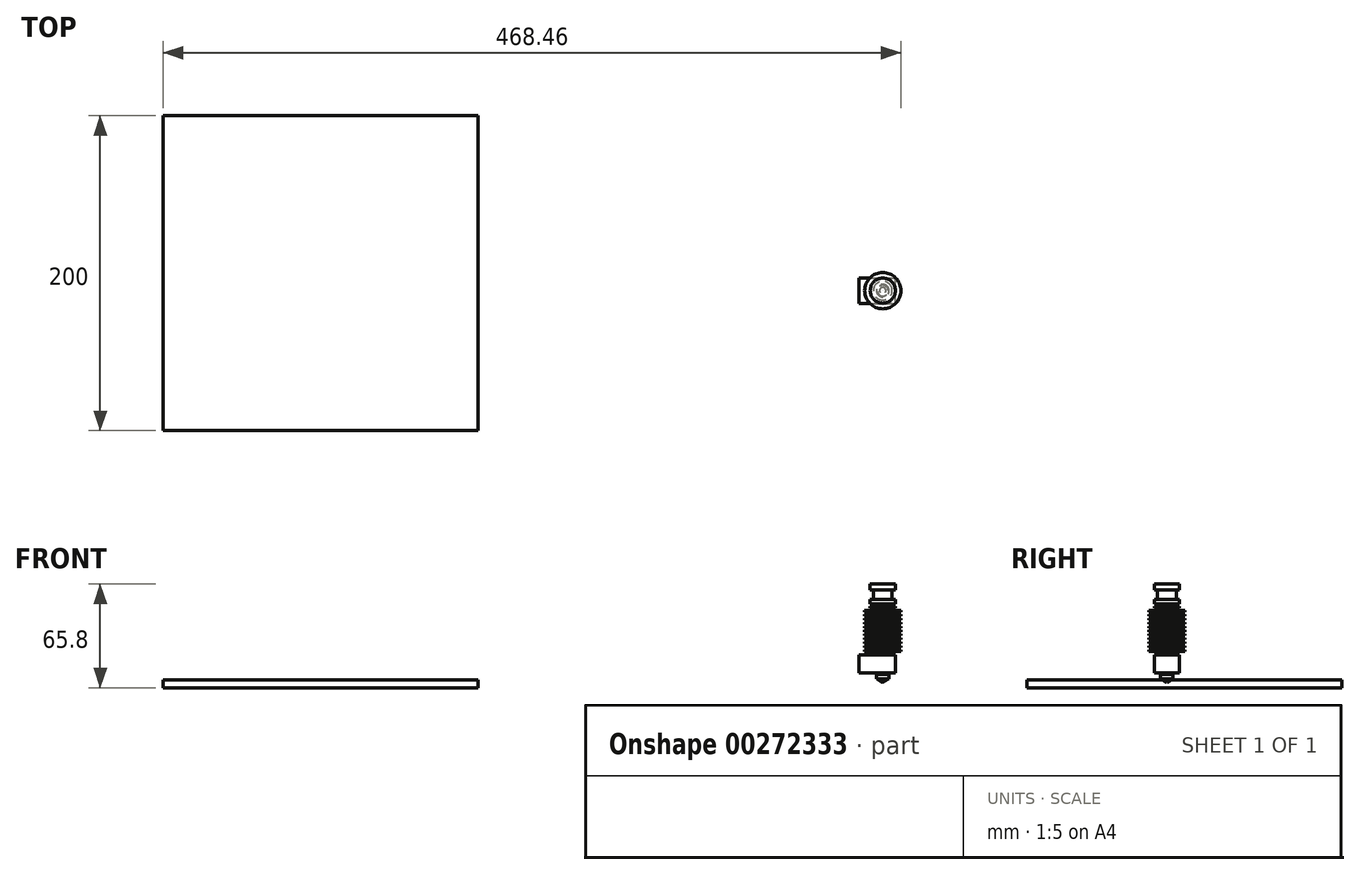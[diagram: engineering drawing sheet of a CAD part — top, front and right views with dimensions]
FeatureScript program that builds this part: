
annotation { "Feature Type Name" : "Feature", "Feature Type Description" : "" }
export const myFeature = defineFeature(function(context is Context, id is Id, definition is map)
    precondition{}
    {
        {
            var Q0;
            Q0=qCreatedBy(makeId("Front.planeOp"),FACE);
            var sketch = newSketch(context, id + "F0", { "sketchPlane" : qUnion([Q0])});
            skLineSegment(sketch, "E0", {"start": v(-127.3, 65.8) * mm, "end": v(-127.3, 23.1) * mm});
            skLineSegment(sketch, "E1", {"start": v(-127.3, 65.8) * mm, "end": v(-119.3, 65.8) * mm});
            skLineSegment(sketch, "E2", {"start": v(-119.3, 65.8) * mm, "end": v(-119.3, 62.1) * mm});
            skLineSegment(sketch, "E3", {"start": v(-119.3, 62.1) * mm, "end": v(-121.3, 62.1) * mm});
            skLineSegment(sketch, "E4", {"start": v(-121.3, 62.1) * mm, "end": v(-121.3, 56.1) * mm});
            skLineSegment(sketch, "E5", {"start": v(-121.3, 56.1) * mm, "end": v(-119.3, 56.1) * mm});
            skLineSegment(sketch, "E6", {"start": v(-119.3, 56.1) * mm, "end": v(-119.3, 53.1) * mm});
            skLineSegment(sketch, "E7", {"start": v(-119.3, 53.1) * mm, "end": v(-121.3, 53.1) * mm});
            skLineSegment(sketch, "E8", {"start": v(-121.3, 53.1) * mm, "end": v(-121.3, 51.6) * mm});
            skLineSegment(sketch, "E9", {"start": v(-121.3, 51.6) * mm, "end": v(-119.3, 51.6) * mm});
            skLineSegment(sketch, "E10", {"start": v(-119.3, 51.6) * mm, "end": v(-119.3, 50.6) * mm});
            skLineSegment(sketch, "E11", {"start": v(-119.3, 50.6) * mm, "end": v(-121.3, 50.6) * mm});
            skLineSegment(sketch, "E12", {"start": v(-121.3, 50.6) * mm, "end": v(-121.3, 49.1) * mm});
            skLineSegment(sketch, "E13", {"start": v(-121.3, 49.1) * mm, "end": v(-115.8, 49.1) * mm});
            skLineSegment(sketch, "E14", {"start": v(-115.8, 49.1) * mm, "end": v(-115.8, 48.1) * mm});
            skLineSegment(sketch, "E15", {"start": v(-115.8, 48.1) * mm, "end": v(-121.3, 48.1) * mm});
            skLineSegment(sketch, "E16.1.0.1", {"start": v(-121.3, 46.6) * mm, "end": v(-115.8, 46.6) * mm});
            skLineSegment(sketch, "E16.1.0.2", {"start": v(-115.8, 46.6) * mm, "end": v(-115.8, 45.6) * mm});
            skLineSegment(sketch, "E16.1.0.3", {"start": v(-115.8, 45.6) * mm, "end": v(-121.3, 45.6) * mm});
            skLineSegment(sketch, "E16.2.0.0", {"start": v(-121.3, 45.6) * mm, "end": v(-121.3, 44.1) * mm});
            skLineSegment(sketch, "E16.2.0.1", {"start": v(-121.3, 44.1) * mm, "end": v(-115.8, 44.1) * mm});
            skLineSegment(sketch, "E16.2.0.2", {"start": v(-115.8, 44.1) * mm, "end": v(-115.8, 43.1) * mm});
            skLineSegment(sketch, "E16.2.0.3", {"start": v(-115.8, 43.1) * mm, "end": v(-121.3, 43.1) * mm});
            skLineSegment(sketch, "E16.direction1", {"start": v(-121.3, 48.1) * mm, "end": v(-121.3, 45.6) * mm, "construction": true});
            skLineSegment(sketch, "E17.0.3.0", {"start": v(-121.3, 43.1) * mm, "end": v(-121.3, 41.6) * mm});
            skLineSegment(sketch, "E17.3.3.0", {"start": v(-121.3, 41.6) * mm, "end": v(-115.8, 41.6) * mm});
            skLineSegment(sketch, "E17.6.3.0", {"start": v(-115.8, 41.6) * mm, "end": v(-115.8, 40.6) * mm});
            skLineSegment(sketch, "E17.9.3.0", {"start": v(-115.8, 40.6) * mm, "end": v(-121.3, 40.6) * mm});
            skLineSegment(sketch, "E17.0.4.0", {"start": v(-121.3, 40.6) * mm, "end": v(-121.3, 39.1) * mm});
            skLineSegment(sketch, "E17.3.4.0", {"start": v(-121.3, 39.1) * mm, "end": v(-115.8, 39.1) * mm});
            skLineSegment(sketch, "E17.6.4.0", {"start": v(-115.8, 39.1) * mm, "end": v(-115.8, 38.1) * mm});
            skLineSegment(sketch, "E17.9.4.0", {"start": v(-115.8, 38.1) * mm, "end": v(-121.3, 38.1) * mm});
            skLineSegment(sketch, "E17.0.5.0", {"start": v(-121.3, 38.1) * mm, "end": v(-121.3, 36.6) * mm});
            skLineSegment(sketch, "E17.3.5.0", {"start": v(-121.3, 36.6) * mm, "end": v(-115.8, 36.6) * mm});
            skLineSegment(sketch, "E17.6.5.0", {"start": v(-115.8, 36.6) * mm, "end": v(-115.8, 35.6) * mm});
            skLineSegment(sketch, "E17.9.5.0", {"start": v(-115.8, 35.6) * mm, "end": v(-121.3, 35.6) * mm});
            skLineSegment(sketch, "E17.0.6.0", {"start": v(-121.3, 35.6) * mm, "end": v(-121.3, 34.1) * mm});
            skLineSegment(sketch, "E17.3.6.0", {"start": v(-121.3, 34.1) * mm, "end": v(-115.8, 34.1) * mm});
            skLineSegment(sketch, "E17.6.6.0", {"start": v(-115.8, 34.1) * mm, "end": v(-115.8, 33.1) * mm});
            skLineSegment(sketch, "E17.9.6.0", {"start": v(-115.8, 33.1) * mm, "end": v(-121.3, 33.1) * mm});
            skLineSegment(sketch, "E17.0.7.0", {"start": v(-121.3, 33.1) * mm, "end": v(-121.3, 31.6) * mm});
            skLineSegment(sketch, "E17.3.7.0", {"start": v(-121.3, 31.6) * mm, "end": v(-115.8, 31.6) * mm});
            skLineSegment(sketch, "E17.6.7.0", {"start": v(-115.8, 31.6) * mm, "end": v(-115.8, 30.6) * mm});
            skLineSegment(sketch, "E17.9.7.0", {"start": v(-115.8, 30.6) * mm, "end": v(-121.3, 30.6) * mm});
            skLineSegment(sketch, "E17.0.8.0", {"start": v(-121.3, 30.6) * mm, "end": v(-121.3, 29.1) * mm});
            skLineSegment(sketch, "E17.3.8.0", {"start": v(-121.3, 29.1) * mm, "end": v(-115.8, 29.1) * mm});
            skLineSegment(sketch, "E17.6.8.0", {"start": v(-115.8, 29.1) * mm, "end": v(-115.8, 28.1) * mm});
            skLineSegment(sketch, "E17.9.8.0", {"start": v(-115.8, 28.1) * mm, "end": v(-121.3, 28.1) * mm});
            skLineSegment(sketch, "E17.0.9.0", {"start": v(-121.3, 28.1) * mm, "end": v(-121.3, 26.6) * mm});
            skLineSegment(sketch, "E17.3.9.0", {"start": v(-121.3, 26.6) * mm, "end": v(-115.8, 26.6) * mm});
            skLineSegment(sketch, "E17.6.9.0", {"start": v(-115.8, 26.6) * mm, "end": v(-115.8, 25.6) * mm});
            skLineSegment(sketch, "E17.9.9.0", {"start": v(-115.8, 25.6) * mm, "end": v(-121.3, 25.6) * mm});
            skLineSegment(sketch, "E18.0.10.0", {"start": v(-121.3, 25.6) * mm, "end": v(-121.3, 24.1) * mm});
            skLineSegment(sketch, "E18.3.10.0", {"start": v(-121.3, 24.1) * mm, "end": v(-115.8, 24.1) * mm});
            skLineSegment(sketch, "E18.6.10.0", {"start": v(-115.8, 24.1) * mm, "end": v(-115.8, 23.1) * mm});
            skLineSegment(sketch, "E18.9.10.0", {"start": v(-115.8, 23.1) * mm, "end": v(-121.3, 23.1) * mm});
            skLineSegment(sketch, "E19", {"start": v(-121.3, 48.1) * mm, "end": v(-121.3, 46.6) * mm});
            skLineSegment(sketch, "E20", {"start": v(-125.26, 23.1) * mm, "end": v(-121.3, 23.1) * mm});
            skLineSegment(sketch, "E21", {"start": v(-127.3, 23.1) * mm, "end": v(-127.3, 21) * mm});
            skLineSegment(sketch, "E22", {"start": v(-127.3, 21) * mm, "end": v(-127.3, 16) * mm});
            skLineSegment(sketch, "E23", {"start": v(-127.3, 16) * mm, "end": v(-127.3, 5.5) * mm});
            skLineSegment(sketch, "E24", {"start": v(-127.3, 5.5) * mm, "end": v(-127.3, 3.5) * mm});
            skLineSegment(sketch, "E25", {"start": v(-127.28, 3.51) * mm, "end": v(-123.84, 5.5) * mm});
            skLineSegment(sketch, "E26", {"start": v(-123.84, 5.5) * mm, "end": v(-127.3, 5.5) * mm, "construction": true});
            skLineSegment(sketch, "E27", {"start": v(-123.84, 5.5) * mm, "end": v(-123.3, 5.5) * mm});
            skLineSegment(sketch, "E28", {"start": v(-123.3, 5.5) * mm, "end": v(-123.3, 8.5) * mm});
            skLineSegment(sketch, "E29", {"start": v(-123.3, 8.5) * mm, "end": v(-123.84, 8.5) * mm});
            skLineSegment(sketch, "E30", {"start": v(-123.84, 8.5) * mm, "end": v(-123.84, 16) * mm});
            skLineSegment(sketch, "E31", {"start": v(-123.84, 16) * mm, "end": v(-124.84, 16) * mm});
            skLineSegment(sketch, "E32", {"start": v(-124.84, 16) * mm, "end": v(-124.84, 21) * mm});
            skLineSegment(sketch, "E33", {"start": v(-124.84, 21) * mm, "end": v(-125.26, 21) * mm});
            skLineSegment(sketch, "E34", {"start": v(-125.26, 21) * mm, "end": v(-125.26, 23.1) * mm});
            skLineSegment(sketch, "E35", {"start": v(-127.3, 3.51) * mm, "end": v(-127.28, 3.51) * mm});
            skSolve(sketch);
        }
        {
            var Q0;
            Q0=makeQuery(id+"F0.imprint","IMPRINT",FACE,{"disambiguationData":[TD([[makeQuery(id+"F0.imprint","IMPRINT",EDGE,{"derivedFrom":sQuery(id+"F0.wireOp",EDGE,"E0")}),1.0]])]});
            var Q1;
            Q1=sQuery(id+"F0.wireOp",EDGE,"E0");
            revolve(context, id + "F1", {"entities" : qUnion([Q0]), "axis" : qUnion([Q1]), "revolveType" : RevolveType.FULL});
        }
        {
            var Q0;
            Q0=qCreatedBy(makeId("Top.planeOp"),FACE);
            var sketch = newSketch(context, id + "F2", { "sketchPlane" : qUnion([Q0])});
            skLineSegment(sketch, "E36.bottom", {"start": v(-384.26, -88.9) * mm, "end": v(-584.26, -88.9) * mm});
            skLineSegment(sketch, "E36.top", {"start": v(-384.26, 111.1) * mm, "end": v(-584.26, 111.1) * mm});
            skLineSegment(sketch, "E36.left", {"start": v(-384.26, -88.9) * mm, "end": v(-384.26, 111.1) * mm});
            skLineSegment(sketch, "E36.right", {"start": v(-584.26, -88.9) * mm, "end": v(-584.26, 111.1) * mm});
            skSolve(sketch);
        }
        {
            var Q0;
            Q0=makeQuery(id+"F2.imprint","IMPRINT",FACE,{"disambiguationData":[TD([[makeQuery(id+"F2.imprint","IMPRINT",EDGE,{"derivedFrom":sQuery(id+"F2.wireOp",EDGE,"E36.bottom")}),-1.0]])]});
            extrude(context, id + "F3", {"entities" : qUnion([Q0]), "depth" : 5 * mm});
        }
        {
            var Q0;
            Q0=makeQuery(id+"F1.opRevolve","SWEPT_FACE",FACE,{"disambiguationData":[OSD([sQuery(id+"F0.wireOp",EDGE,"E33")])]});
            cPlane(context, id + "F4", {"entities" : qUnion([Q0]), "cplaneType" : CPlaneType.OFFSET, "offset" : 0 * mm, "width" : 150 * mm, "height" : 150 * mm});
        }
        {
            var Q0;
            Q0=qCreatedBy(id+"F4.planeOp",FACE);
            var sketch = newSketch(context, id + "F5", { "sketchPlane" : qUnion([Q0])});
            skLineSegment(sketch, "E37.bottom", {"start": v(-142.3, -8) * mm, "end": v(-119.3, -8) * mm});
            skLineSegment(sketch, "E37.top", {"start": v(-142.3, 8) * mm, "end": v(-119.3, 8) * mm});
            skLineSegment(sketch, "E37.left", {"start": v(-142.3, -8) * mm, "end": v(-142.3, 8) * mm});
            skLineSegment(sketch, "E37.right", {"start": v(-119.3, -8) * mm, "end": v(-119.3, 8) * mm});
            skPoint(sketch, "E38", {"position": v(-127.3, 0) * mm});
            skLineSegment(sketch, "E39", {"start": v(-119.3, 0) * mm, "end": v(-127.3, 0) * mm});
            skSolve(sketch);
        }
        {
            var Q0;
            {var subQ1=sQuery(id+"F5.wireOp",EDGE,"E37.bottom");Q0=makeQuery(id+"F5.imprint","IMPRINT",FACE,{"disambiguationData":[TD([[makeQuery(id+"F5.imprint","IMPRINT",EDGE,{"derivedFrom":subQ1}),1.0]])]});}
            extrude(context, id + "F6", {"entities" : qUnion([Q0]), "operationType" : NewBodyOperationType.ADD, "oppositeDirection" : true, "depth" : 11.5 * mm});
        }
        {
            var Q0;
            Q0=makeQuery(id+"F1.opRevolve","SWEPT_FACE",FACE,{"disambiguationData":[OSD([sQuery(id+"F0.wireOp",EDGE,"E35")])]});
            var sketch = newSketch(context, id + "F7", { "sketchPlane" : qUnion([Q0])});
            skPoint(sketch, "E40", {"position": v(-127.3, 0) * mm});
            skLineSegment(sketch, "E41.bottom", {"start": v(-127.3, 0) * mm, "end": v(-127.3, 0) * mm});
            skLineSegment(sketch, "E41.top", {"start": v(-127.3, 0) * mm, "end": v(-127.3, 0) * mm});
            skLineSegment(sketch, "E41.left", {"start": v(-127.3, 0) * mm, "end": v(-127.3, 0) * mm});
            skLineSegment(sketch, "E41.right", {"start": v(-127.3, 0) * mm, "end": v(-127.3, 0) * mm});
            skLineSegment(sketch, "E42", {"start": v(-127.3, 0) * mm, "end": v(-127.3, 0) * mm, "construction": true});
            skSolve(sketch);
        }
        {
            var Q0;
            Q0=makeQuery(id+"F7.imprint","IMPRINT",FACE,{"disambiguationData":[TD([[makeQuery(id+"F7.imprint","IMPRINT",EDGE,{"derivedFrom":sQuery(id+"F7.wireOp",EDGE,"E41.bottom")}),-1.0]])]});
            extrude(context, id + "F8", {"entities" : qUnion([Q0]), "operationType" : NewBodyOperationType.ADD, "depth" : 0.01 * mm});
        }
    });
